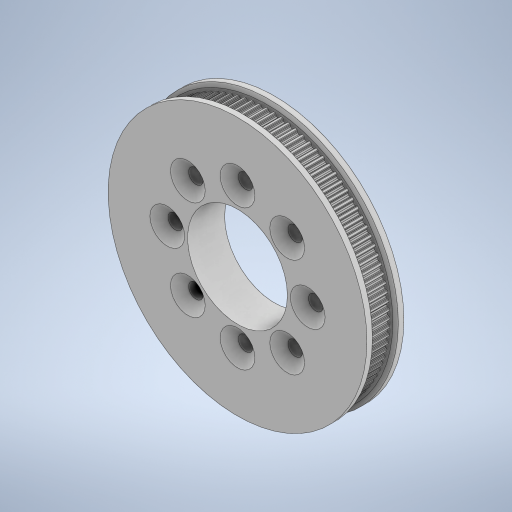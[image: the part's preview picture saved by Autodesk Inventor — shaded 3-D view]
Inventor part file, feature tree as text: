
AUTODESK INVENTOR PART (.ipt)
format: ipt  version: 2024 (Build 280153000, 153)  size: 3,483,136 bytes
history: native  units: mm
features: extrude x4, sketch x3, chamfer x2, projected_geometry x2, pattern_circular x1, mirror x1
ambient origin geometry x8: Origin, YZ Plane, XZ Plane, XY Plane, X Axis, Y Axis, Z Axis, Center Point
bodies: Solid1 (feature_tree)
feature tree (13):
  extrude  "Extrusion1"  Depth=0.298507mm
  pattern_circular  "Circular Pattern1"  [2 undecoded]
  extrude  "Extrusion2"  Depth=0.555mm
  chamfer  "Chamfer1"  Distance=1.0mm
  mirror  "Mirror1"
  extrude  "Extrusion5"  Depth=0.15mm
  extrude  "Extrusion6"  Depth=0.6mm
  chamfer  "Chamfer2"  Distance=6.0mm
  sketch  "Sketch1"  dims[d0=67.0mm d1=0.298507mm]
  sketch  "Sketch6"  dims[d2=0.119403mm]
  projected_geometry  "Projected Loop2"
  sketch  "Sketch7"  dims[d3=1.004mm d4=0.75mm d5=0.555mm d6=1.0mm d7=0.15mm d9=0.6mm d10=6.0mm d11=0.0mm d12=1052.433539mm d13=360.0deg d15=70.0mm d16=2.0mm d17=0.0mm d18=1.0mm d19=0.5mm d20=45.0deg d21=5.0mm d31=27.0mm d32=0.0mm d33=0.0mm d34=19.0mm d35=4.0mm d36=80.0mm d38=360.0deg d40=0.0mm d41=0.0mm d42=2.7mm d43=2.2mm d44=45.0deg]
  projected_geometry  "Projected Loop3"
note: 2 required parameter values undecoded (feature->parameter linkage not recoverable at this tier; creation-order binding heuristic only, values carry confidence <= 0.55)
